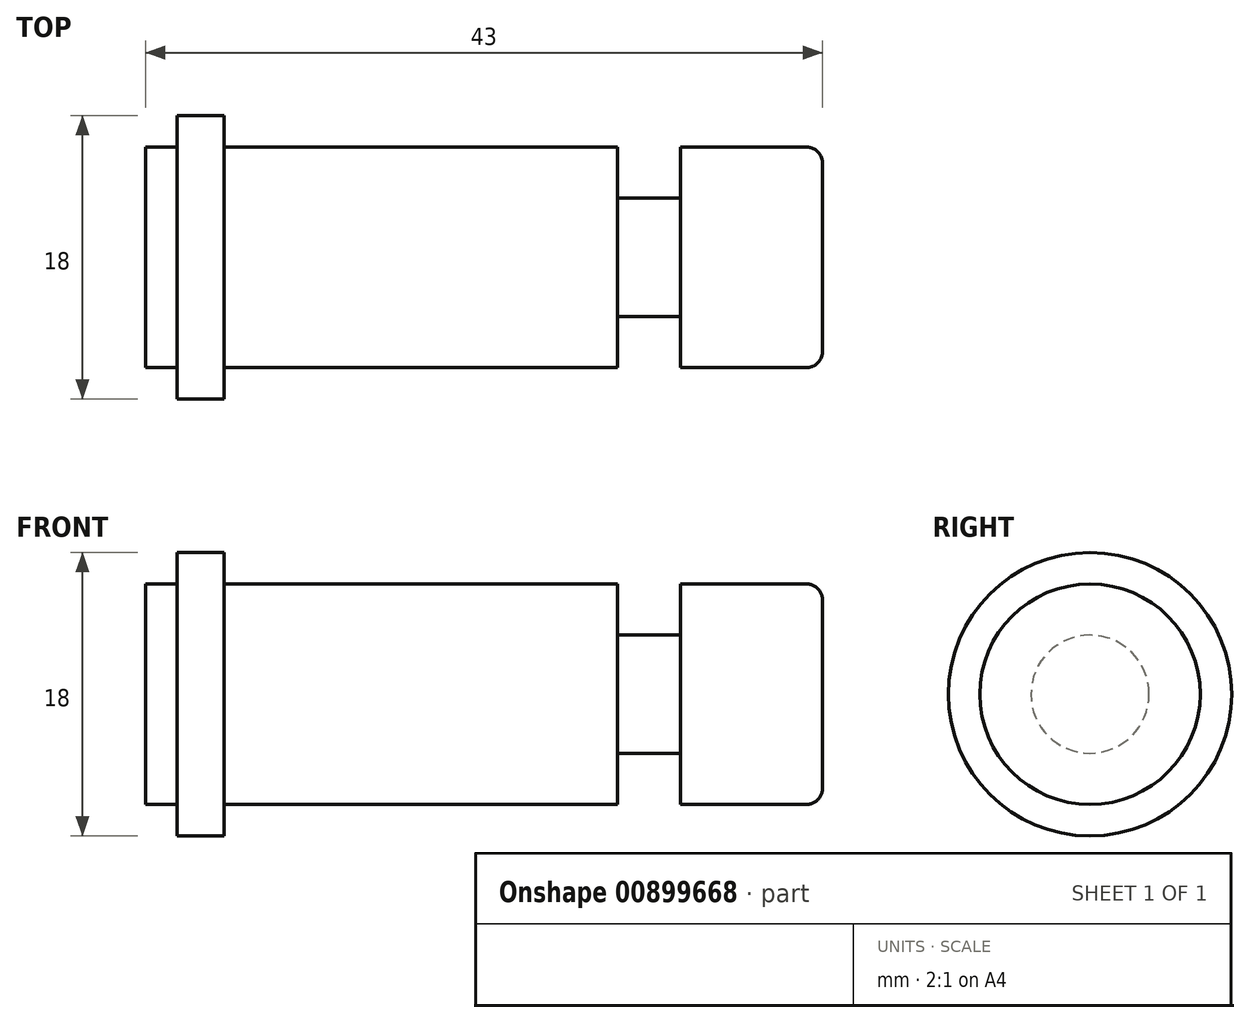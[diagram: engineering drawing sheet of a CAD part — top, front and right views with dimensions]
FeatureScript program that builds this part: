
annotation { "Feature Type Name" : "Feature", "Feature Type Description" : "" }
export const myFeature = defineFeature(function(context is Context, id is Id, definition is map)
    precondition{}
    {
        {
            var Q0;
            Q0=qCreatedBy(makeId("Front.planeOp"),FACE);
            var sketch = newSketch(context, id + "F0", { "sketchPlane" : qUnion([Q0])});
            skLineSegment(sketch, "E0", {"start": v(0, 0) * mm, "end": v(0, 7) * mm});
            skLineSegment(sketch, "E1", {"start": v(0, 7) * mm, "end": v(2, 7) * mm});
            skLineSegment(sketch, "E2", {"start": v(5, 7) * mm, "end": v(30, 7) * mm});
            skLineSegment(sketch, "E3", {"start": v(30, 7) * mm, "end": v(30, 3.75) * mm});
            skLineSegment(sketch, "E4", {"start": v(30, 3.75) * mm, "end": v(34, 3.75) * mm});
            skLineSegment(sketch, "E5", {"start": v(34, 3.75) * mm, "end": v(34, 7) * mm});
            skLineSegment(sketch, "E6", {"start": v(34, 7) * mm, "end": v(43, 7) * mm});
            skLineSegment(sketch, "E7", {"start": v(43, 7) * mm, "end": v(43, 0) * mm});
            skLineSegment(sketch, "E8", {"start": v(0, 0) * mm, "end": v(43, 0) * mm});
            skLineSegment(sketch, "E9", {"start": v(5, 7) * mm, "end": v(5, 9) * mm});
            skLineSegment(sketch, "E10", {"start": v(5, 9) * mm, "end": v(2, 9) * mm});
            skLineSegment(sketch, "E11", {"start": v(2, 9) * mm, "end": v(2, 7) * mm});
            skPoint(sketch, "E12.orphan", {"position": v(4.93, 7) * mm});
            skSolve(sketch);
        }
        {
            var Q0;
            Q0=makeQuery(id+"F0.imprint","IMPRINT",FACE,{"disambiguationData":[TD([[makeQuery(id+"F0.imprint","IMPRINT",EDGE,{"derivedFrom":sQuery(id+"F0.wireOp",EDGE,"E0")}),-1.0]])]});
            var Q1;
            Q1=sQuery(id+"F0.wireOp",EDGE,"E8");
            revolve(context, id + "F1", {"surfaceOperationType" : NewSurfaceOperationType.NEW, "entities" : qUnion([Q0]), "axis" : qUnion([Q1]), "revolveType" : RevolveType.FULL});
        }
        {
            var Q0;
            Q0=makeQuery(id+"F1.opRevolve","SWEPT_FACE",FACE,{"disambiguationData":[OSD([sQuery(id+"F0.wireOp",EDGE,"E7")])]});
            fillet(context, id + "F2", {"entities" : qUnion([Q0]), "radius" : 1 * mm, "tangentPropagation" : true, "allowEdgeOverflow" : false});
        }
    });
